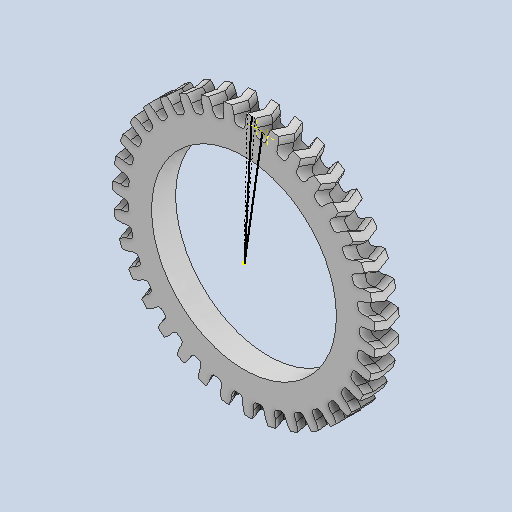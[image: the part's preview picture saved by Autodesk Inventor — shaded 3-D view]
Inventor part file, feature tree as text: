
AUTODESK INVENTOR PART (.ipt)
format: ipt  version: 2022 (Build 260153070, 153G)  size: 1,445,376 bytes
history: native  units: mm
features: sketch x3, extrude x2, helix x1, pattern_circular x1, mirror x1
ambient origin geometry x8: Origin, YZ Plane, XZ Plane, XY Plane, X Axis, Y Axis, Z Axis, Center Point
bodies: Solid1 (feature_tree)
feature tree (8):
  sketch  "Sketch1"  dims[d0=1.5mm d1=0.0mm]
  extrude  "Extrusion1"  TaperAngle=0.0deg  [1 undecoded]
  helix  "Coil1"  [1 undecoded]
  pattern_circular  "Circular Pattern1"  [2 undecoded]
  mirror  "Mirror1"
  extrude  "Extrusion2"  [1 undecoded]
  sketch  "Sketch4"  dims[d13=23.05mm d14=10.0mm d15=0.0mm]
  sketch  "Sketch3"  dims[d2=273.26323mm d3=1.5mm d4=10.0mm d5=0.0mm d6=90.0deg d7=90.0deg d8=0.0mm d9=0.0mm d10=350.0mm d11=360.0deg]
note: 5 required parameter values undecoded (feature->parameter linkage not recoverable at this tier; creation-order binding heuristic only, values carry confidence <= 0.55)
